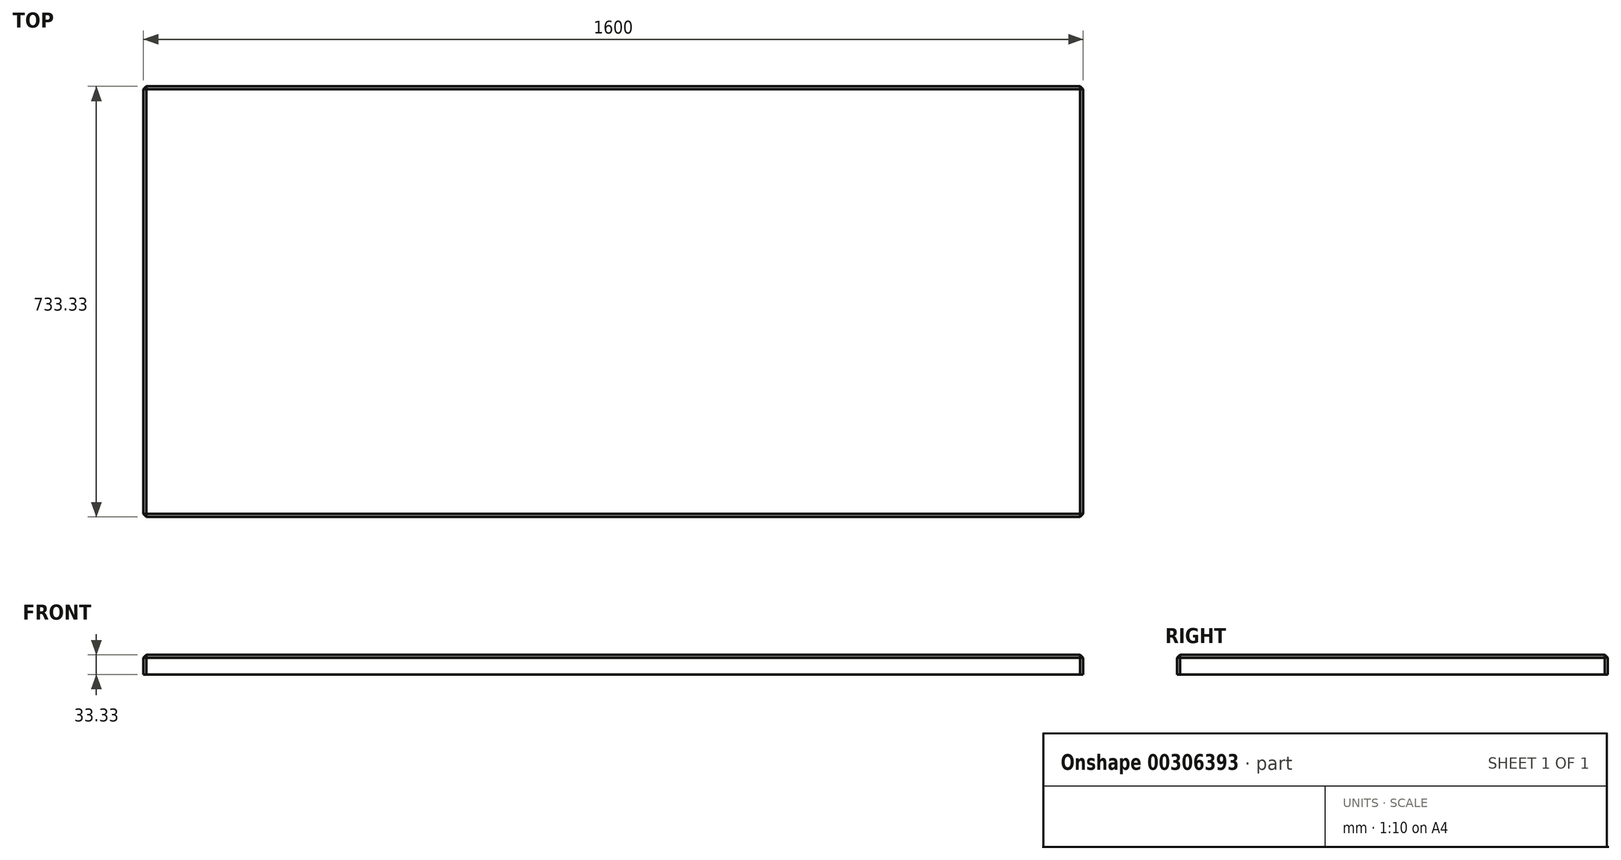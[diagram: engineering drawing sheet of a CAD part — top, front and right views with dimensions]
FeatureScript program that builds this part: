
annotation { "Feature Type Name" : "Feature", "Feature Type Description" : "" }
export const myFeature = defineFeature(function(context is Context, id is Id, definition is map)
    precondition{}
    {
        {
            var Q0;
            Q0=qCreatedBy(makeId("Front.planeOp"),FACE);
            var sketch = newSketch(context, id + "F0", { "sketchPlane" : qUnion([Q0])});
            skLineSegment(sketch, "E0.bottom", {"start": v(-281.48, 0) * mm, "end": v(1318.52, 0) * mm});
            skLineSegment(sketch, "E0.top", {"start": v(-281.48, 33.33) * mm, "end": v(1318.52, 33.33) * mm});
            skLineSegment(sketch, "E0.left", {"start": v(-281.48, 0) * mm, "end": v(-281.48, 33.33) * mm});
            skLineSegment(sketch, "E0.right", {"start": v(1318.52, 0) * mm, "end": v(1318.52, 33.33) * mm});
            skSolve(sketch);
        }
        {
            var Q0;
            Q0 = qSketchRegion(id + "F0", true);
            extrude(context, id + "F1", {"entities" : qUnion([Q0]), "depth" : 733.33 * mm});
        }
        {
            var Q0;
            Q0=makeQuery(id+"F1.opExtrude","CAP_EDGE",EDGE,{"disambiguationData":[OSD([sQuery(id+"F0.wireOp",EDGE,"E0.top")])],"isStart":true});
            var Q1;
            Q1=makeQuery(id+"F1.opExtrude","SWEPT_FACE",FACE,{"disambiguationData":[OSD([sQuery(id+"F0.wireOp",EDGE,"E0.top")])]});
            var Q2;
            Q2=makeQuery(id+"F1.opExtrude","CAP_EDGE",EDGE,{"disambiguationData":[OSD([sQuery(id+"F0.wireOp",EDGE,"E0.right")])],"isStart":false});
            var Q3;
            Q3=makeQuery(id+"F1.opExtrude","CAP_EDGE",EDGE,{"disambiguationData":[OSD([sQuery(id+"F0.wireOp",EDGE,"E0.right")])],"isStart":true});
            var Q4;
            Q4=makeQuery(id+"F1.opExtrude","CAP_EDGE",EDGE,{"disambiguationData":[OSD([sQuery(id+"F0.wireOp",EDGE,"E0.left")])],"isStart":false});
            var Q5;
            Q5=makeQuery(id+"F1.opExtrude","CAP_EDGE",EDGE,{"disambiguationData":[OSD([sQuery(id+"F0.wireOp",EDGE,"E0.left")])],"isStart":true});
            chamfer(context, id + "F2", {"entities" : qUnion([Q0, Q1, Q2, Q3, Q4, Q5]), "width" : 5 * mm, "tangentPropagation" : true});
        }
    });
